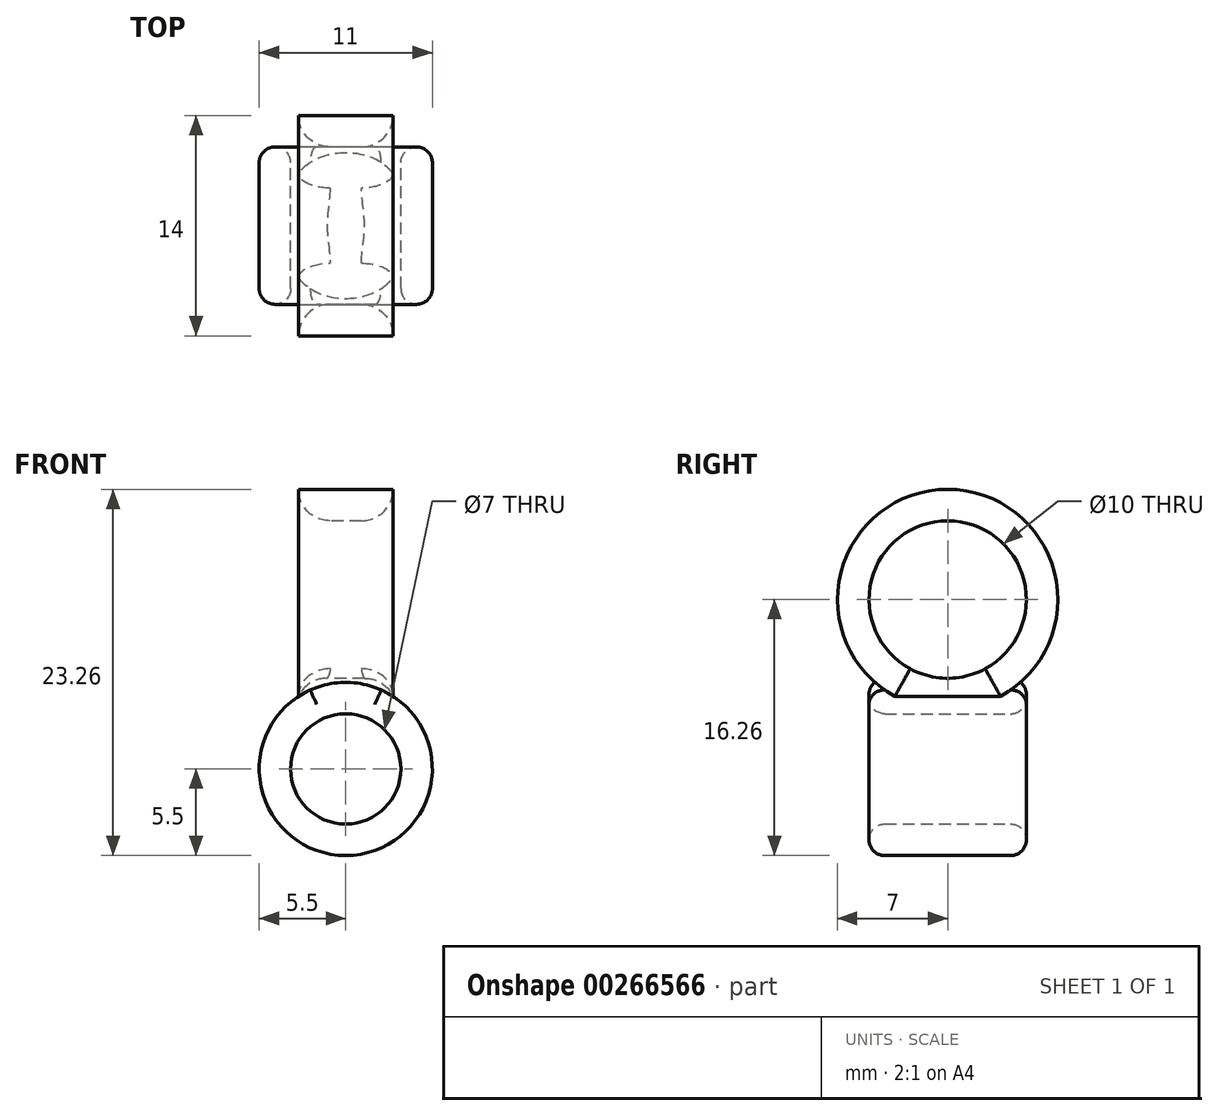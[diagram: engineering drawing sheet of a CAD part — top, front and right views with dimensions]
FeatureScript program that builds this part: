
annotation { "Feature Type Name" : "Feature", "Feature Type Description" : "" }
export const myFeature = defineFeature(function(context is Context, id is Id, definition is map)
    precondition{}
    {
        {
            var Q0;
            Q0=qCreatedBy(makeId("Front.planeOp"),FACE);
            var sketch = newSketch(context, id + "F0", { "sketchPlane" : qUnion([Q0])});
            skCircle(sketch, "E0", {"center": v(0, 0) * mm, "radius": 3.5 * mm});
            skCircle(sketch, "E1.0", {"center": v(0, 0) * mm, "radius": 5.5 * mm});
            skSolve(sketch);
        }
        {
            var Q0;
            Q0 = qSketchRegion(id + "F0", true);
            extrude(context, id + "F1", {"entities" : qUnion([Q0]), "depth" : 10 * mm, "symmetric" : true});
        }
        {
            var Q0;
            Q0=qCreatedBy(makeId("Right.planeOp"),FACE);
            cPlane(context, id + "F2", {"entities" : qUnion([Q0]), "cplaneType" : CPlaneType.OFFSET, "offset" : 5.5 * mm, "width" : 150 * mm, "height" : 150 * mm});
        }
        {
            var Q0;
            Q0=qCreatedBy(makeId("Right.planeOp"),FACE);
            var sketch = newSketch(context, id + "F3", { "sketchPlane" : qUnion([Q0])});
            skCircle(sketch, "E2", {"center": v(0, 10.76) * mm, "radius": 7 * mm});
            skCircle(sketch, "E3", {"center": v(0, 10.76) * mm, "radius": 5 * mm});
            skSolve(sketch);
        }
        {
            var Q0;
            Q0 = qSketchRegion(id + "F3", true);
            extrude(context, id + "F4", {"entities" : qUnion([Q0]), "operationType" : NewBodyOperationType.ADD, "depth" : 6 * mm, "symmetric" : true});
        }
        {
            var Q0;
            Q0=makeQuery(id+"F1.opExtrude","CAP_FACE",FACE,{"disambiguationData":[OSD([sQuery(id+"F0.wireOp",EDGE,"E0"),sQuery(id+"F0.wireOp",EDGE,"E1.0")])],"isStart":false});
            var Q1;
            Q1=makeQuery(id+"F1.opExtrude","CAP_FACE",FACE,{"disambiguationData":[OSD([sQuery(id+"F0.wireOp",EDGE,"E0"),sQuery(id+"F0.wireOp",EDGE,"E1.0")])],"isStart":true});
            fillet(context, id + "F5", {"entities" : qUnion([Q0, Q1]), "radius" : 1 * mm, "tangentPropagation" : true, "allowEdgeOverflow" : false});
        }
        {
            var Q0;
            Q0=makeQuery(id+"F4.opExtrude","CAP_EDGE",EDGE,{"disambiguationData":[OSD([sQuery(id+"F3.wireOp",EDGE,"E3")])],"isStart":true});
            var Q1;
            Q1=makeQuery(id+"F4.opExtrude","CAP_EDGE",EDGE,{"disambiguationData":[OSD([sQuery(id+"F3.wireOp",EDGE,"E3")])],"isStart":false});
            fillet(context, id + "F6", {"entities" : qUnion([Q0, Q1]), "radius" : 2 * mm, "tangentPropagation" : true, "allowEdgeOverflow" : false});
        }
    });
